# Revit family: SOT_Turano_Multiproduct_BIM_GB_R4321;R4322;R4323;R4324
name_source: partatom
category: Plumbing Fixtures
revit_build: Autodesk Revit MEP 2014 (Build: 20130308_1515(x64)
units: mm (PartAtom-declared; Revit-internal decimal feet)

## types (20) — shared parameters
Accessories = www.idealspec.co.uk
AreaUnits = millimeters
Assembly Code = C1030200
AssetType = Fixed
BREEAM = No
Brand = Ideal Standard
Category = Furniture
CodePerformance = EN 14749:2005
ConnectionType = Plumbing
Default Elevation = 800 mm  [stored 2.62467 ft]
DurationUnit = year
ECA = No
ExpectedLife = 30
Features = Work top
IfcExportAs = IfcFurnitureType
IfcExportType = USERDEFINED
InstallationInstructions = www.idealspec.co.uk/resources.html
LinearUnits = millimeters
ManufacturerURL = www.idealspec.co.uk
NBSDescription = Bathroom integrated duct work
NBSReference = 45-35-72/320
NominalDepth = 444 mm
NominalHeight = 12 mm  [stored 0.0393701 ft]
NominalLength = 444 mm
Shape = Rectangular
Space = Internal
SpareParts = www.fastpart-spares.co.uk
TMV3 = No
URL = www.idealspec.co.uk
Uniclass2015Description = Bathroom integrated duct work
Uniclass2015Reference = Pr_40_30_78_04
Uniclass2015Version = Products v1.1
Version = 1
VolumeUnits = Litres
WRAS = No
WarrantyDescription = Manufacturers Warranty
WarrantyDurationParts = 5
WarrantyDurationUnit = year
WaterEfficientProduct = No
zero-valued in all types: CWFU, Cost, HWFU

## per-type parameters (varying)
| type | BIMObjectName | Color | Description | Finish | Model | ModelNumber | ModelReference | Name | NettWeight | NominalWidth | ProductInformation | ShelfMatl | Size |
| R4324WG - Turano 1200mm worktop White Gloss | ISI_IdealStandard_Furniture_Turano_R4324WG | White Gloss | Turano 1200mm worktop | WhiteGlossWG | R4324WG | R4324WG | Turano 1200mm worktop | Furniture_Turano_R4324WG_IdealStandard | 5 Kg | 1200 mm | www.idealspec.co.uk/datasheets/R4324WG | ISI_IdealStandard_Sanitaryware_WhiteGlossWG_Render | 1200 x 444 x 12 mm |
| R4323WG - Turano 1000mm worktop White Gloss | ISI_IdealStandard_Furniture_Turano_R4323WG | White Gloss | Turano 1000mm worktop | WhiteGlossWG | R4323WG | R4323WG | Turano 1000mm worktop | Furniture_Turano_R4323WG_IdealStandard | 4.5 Kg | 1000 mm  [stored 3.28084 ft] | www.idealspec.co.uk/datasheets/R4323WG | ISI_IdealStandard_Sanitaryware_WhiteGlossWG_Render | 1000 x 444 x 12 mm |
| R4322WG - Turano 800mm worktop White Gloss | ISI_IdealStandard_Furniture_Turano_R4322WG | White Gloss | Turano 800mm worktop | WhiteGlossWG | R4322WG | R4322WG | Turano 800mm worktop | Furniture_Turano_R4322WG_IdealStandard | 4 Kg | 800 mm  [stored 2.62467 ft] | www.idealspec.co.uk/datasheets/R4322WG | ISI_IdealStandard_Sanitaryware_WhiteGlossWG_Render | 800 x 444 x 12 mm |
| R4324FF - Turano 1200mm worktop Wood Light Brown | ISI_IdealStandard_Furniture_Turano_R4324FF | Wood Light Brown | Turano 1200mm worktop | WoodLightBrownFF | R4324FF | R4324FF | Turano 1200mm worktop | Furniture_Turano_R4324FF_IdealStandard | 5 Kg | 1200 mm | www.idealspec.co.uk/datasheets/R4324FF | ISI_IdealStandard_Sanitaryware_WoodLightBrownFF_Render | 1200 x 444 x 12 mm |
| R4323FF - Turano 1000mm worktop Wood Light Brown | ISI_IdealStandard_Furniture_Turano_R4323FF | Wood Light Brown | Turano 1000mm worktop | WoodLightBrownFF | R4323FF | R4323FF | Turano 1000mm worktop | Furniture_Turano_R4323FF_IdealStandard | 4.5 Kg | 1000 mm  [stored 3.28084 ft] | www.idealspec.co.uk/datasheets/R4323FF | ISI_IdealStandard_Sanitaryware_WoodLightBrownFF_Render | 1000 x 444 x 12 mm |
| R4322FF - Turano 800mm worktop Wood Light Brown | ISI_IdealStandard_Furniture_Turano_R4322FF | Wood Light Brown | Turano 800mm worktop | WoodLightBrownFF | R4322FF | R4322FF | Turano 800mm worktop | Furniture_Turano_R4322FF_IdealStandard | 4 Kg | 800 mm  [stored 2.62467 ft] | www.idealspec.co.uk/datasheets/R4322FF | ISI_IdealStandard_Sanitaryware_WoodLightBrownFF_Render | 800 x 444 x 12 mm |
| R4324FE - Turano 1200mm worktop Wood Light Grey | ISI_IdealStandard_Furniture_Turano_R4324FE | Wood Light Grey | Turano 1200mm worktop | WoodLightGreyFE | R4324FE | R4324FE | Turano 1200mm worktop | Furniture_Turano_R4324FE_IdealStandard | 5 Kg | 1200 mm | www.idealspec.co.uk/datasheets/R4324FE | ISI_IdealStandard_Sanitaryware_WoodLightGreyFE_Render | 1200 x 444 x 12 mm |
| R4323FE - Turano 1000mm worktop Wood Light Grey | ISI_IdealStandard_Furniture_Turano_R4323FE | Wood Light Grey | Turano 1000mm worktop | WoodLightGreyFE | R4323FE | R4323FE | Turano 1000mm worktop | Furniture_Turano_R4323FE_IdealStandard | 4.5 Kg | 1000 mm  [stored 3.28084 ft] | www.idealspec.co.uk/datasheets/R4323FE | ISI_IdealStandard_Sanitaryware_WoodLightGreyFE_Render | 1000 x 444 x 12 mm |
| R4322FE - Turano 800mm worktop Wood Light Grey | ISI_IdealStandard_Furniture_Turano_R4322FE | Wood Light Grey | Turano 800mm worktop | WoodLightGreyFE | R4322FE | R4322FE | Turano 800mm worktop | Furniture_Turano_R4322FE_IdealStandard | 4 Kg | 800 mm  [stored 2.62467 ft] | www.idealspec.co.uk/datasheets/R4322FE | ISI_IdealStandard_Sanitaryware_WoodLightGreyFE_Render | 800 x 444 x 12 mm |
| R4324FC - Turano 1200mm worktop Gloss Light Brown | ISI_IdealStandard_Furniture_Turano_R4324FC | Gloss Light Brown | Turano 1200mm worktop | GlossLightBrownFC | R4324FC | R4324FC | Turano 1200mm worktop | Furniture_Turano_R4324FC_IdealStandard | 5 Kg | 1200 mm | www.idealspec.co.uk/datasheets/R4324FC | ISI_IdealStandard_Sanitaryware_GlossLightBrownFC_Render | 1200 x 444 x 12 mm |
| R4323FC - Turano 1000mm worktop Gloss Light Brown | ISI_IdealStandard_Furniture_Turano_R4323FC | Gloss Light Brown | Turano 1000mm worktop | GlossLightBrownFC | R4323FC | R4323FC | Turano 1000mm worktop | Furniture_Turano_R4323FC_IdealStandard | 4.5 Kg | 1000 mm  [stored 3.28084 ft] | www.idealspec.co.uk/datasheets/R4323FC | ISI_IdealStandard_Sanitaryware_GlossLightBrownFC_Render | 1000 x 444 x 12 mm |
| R4322FC - Turano 800mm worktop Gloss Light Brown | ISI_IdealStandard_Furniture_Turano_R4322FC | Gloss Light Brown | Turano 800mm worktop | GlossLightBrownFC | R4322FC | R4322FC | Turano 800mm worktop | Furniture_Turano_R4322FC_IdealStandard | 4 Kg | 800 mm  [stored 2.62467 ft] | www.idealspec.co.uk/datasheets/R4322FC | ISI_IdealStandard_Sanitaryware_GlossLightBrownFC_Render | 800 x 444 x 12 mm |
| R4324FA - Turano 1200mm worktop Gloss Light Grey | ISI_IdealStandard_Furniture_Turano_R4324FA | Gloss Light Grey | Turano 1200mm worktop | GlossLightGreyFA | R4324FA | R4324FA | Turano 1200mm worktop | Furniture_Turano_R4324FA_IdealStandard | 5 Kg | 1200 mm | www.idealspec.co.uk/datasheets/R4324FA | ISI_IdealStandard_Sanitaryware_GlossLightGreyFA_Render | 1200 x 444 x 12 mm |
| R4323FA - Turano 1000mm worktop Gloss Light Grey | ISI_IdealStandard_Furniture_Turano_R4323FA | Gloss Light Grey | Turano 1000mm worktop | GlossLightGreyFA | R4323FA | R4323FA | Turano 1000mm worktop | Furniture_Turano_R4323FA_IdealStandard | 4.5 Kg | 1000 mm  [stored 3.28084 ft] | www.idealspec.co.uk/datasheets/R4323FA | ISI_IdealStandard_Sanitaryware_GlossLightGreyFA_Render | 1000 x 444 x 12 mm |
| R4322FA - Turano 800mm worktop Gloss Light Grey | ISI_IdealStandard_Furniture_Turano_R4322FA | Gloss Light Grey | Turano 800mm worktop | GlossLightGreyFA | R4322FA | R4322FA | Turano 800mm worktop | Furniture_Turano_R4322FA_IdealStandard | 4 Kg | 800 mm  [stored 2.62467 ft] | www.idealspec.co.uk/datasheets/R4322FA | ISI_IdealStandard_Sanitaryware_GlossLightGreyFA_Render | 800 x 444 x 12 mm |
| R4321FF - Turano 600mm worktop Wood Light Brown | ISI_IdealStandard_Furniture_Turano_R4321FF | Wood Light Brown | Turano 600mm worktop | WoodLightBrownFF | R4321FF | R4321FF | Turano 600mm worktop | Furniture_Turano_R4321FF_IdealStandard | 3.5 Kg | 600 mm | www.idealspec.co.uk/datasheets/R4321FF | ISI_IdealStandard_Sanitaryware_WoodLightBrownFF_Render | 600 x 444 x 12 mm |
| R4321FC - Turano 600mm worktop Gloss Light Brown | ISI_IdealStandard_Furniture_Turano_R4321FC | Gloss Light Brown | Turano 600mm worktop | GlossLightBrownFC | R4321FC | R4321FC | Turano 600mm worktop | Furniture_Turano_R4321FC_IdealStandard | 3.5 Kg | 600 mm | www.idealspec.co.uk/datasheets/R4321FC | ISI_IdealStandard_Sanitaryware_GlossLightBrownFC_Render | 600 x 444 x 12 mm |
| R4321FA - Turano 600mm worktop Gloss Light Grey | ISI_IdealStandard_Furniture_Turano_R4321FA | Gloss Light Grey | Turano 600mm worktop | GlossLightGreyFA | R4321FA | R4321FA | Turano 600mm worktop | Furniture_Turano_R4321FA_IdealStandard | 3.5 Kg | 600 mm | www.idealspec.co.uk/datasheets/R4321FA | ISI_IdealStandard_Sanitaryware_GlossLightGreyFA_Render | 600 x 444 x 12 mm |
| R4321FE - Turano 600mm worktop Wood Light Grey | ISI_IdealStandard_Furniture_Turano_R4321FE | Wood Light Grey | Turano 600mm worktop | WoodLightGreyFE | R4321FE | R4321FE | Turano 600mm worktop | Furniture_Turano_R4321FE_IdealStandard | 3.5 Kg | 600 mm | www.idealspec.co.uk/datasheets/R4321FE | ISI_IdealStandard_Sanitaryware_WoodLightGreyFE_Render | 600 x 444 x 12 mm |
| R4321WG - Turano 600mm worktop White Gloss | ISI_IdealStandard_Furniture_Turano_R4321WG | White Gloss | Turano 600mm worktop | WhiteGlossWG | R4321WG | R4321WG | Turano 600mm worktop | Furniture_Turano_R4321WG_IdealStandard | 3.5 Kg | 600 mm | www.idealspec.co.uk/datasheets/R4321WG | ISI_IdealStandard_Sanitaryware_WhiteGlossWG_Render | 600 x 444 x 12 mm |

note: [stored X ft] marks values corroborated as IEEE doubles in the binary element streams (Revit-internal decimal feet)

## geometry (parser evidence)
native form markers: Sweep x1
no freeform markers — native parametric forms only
